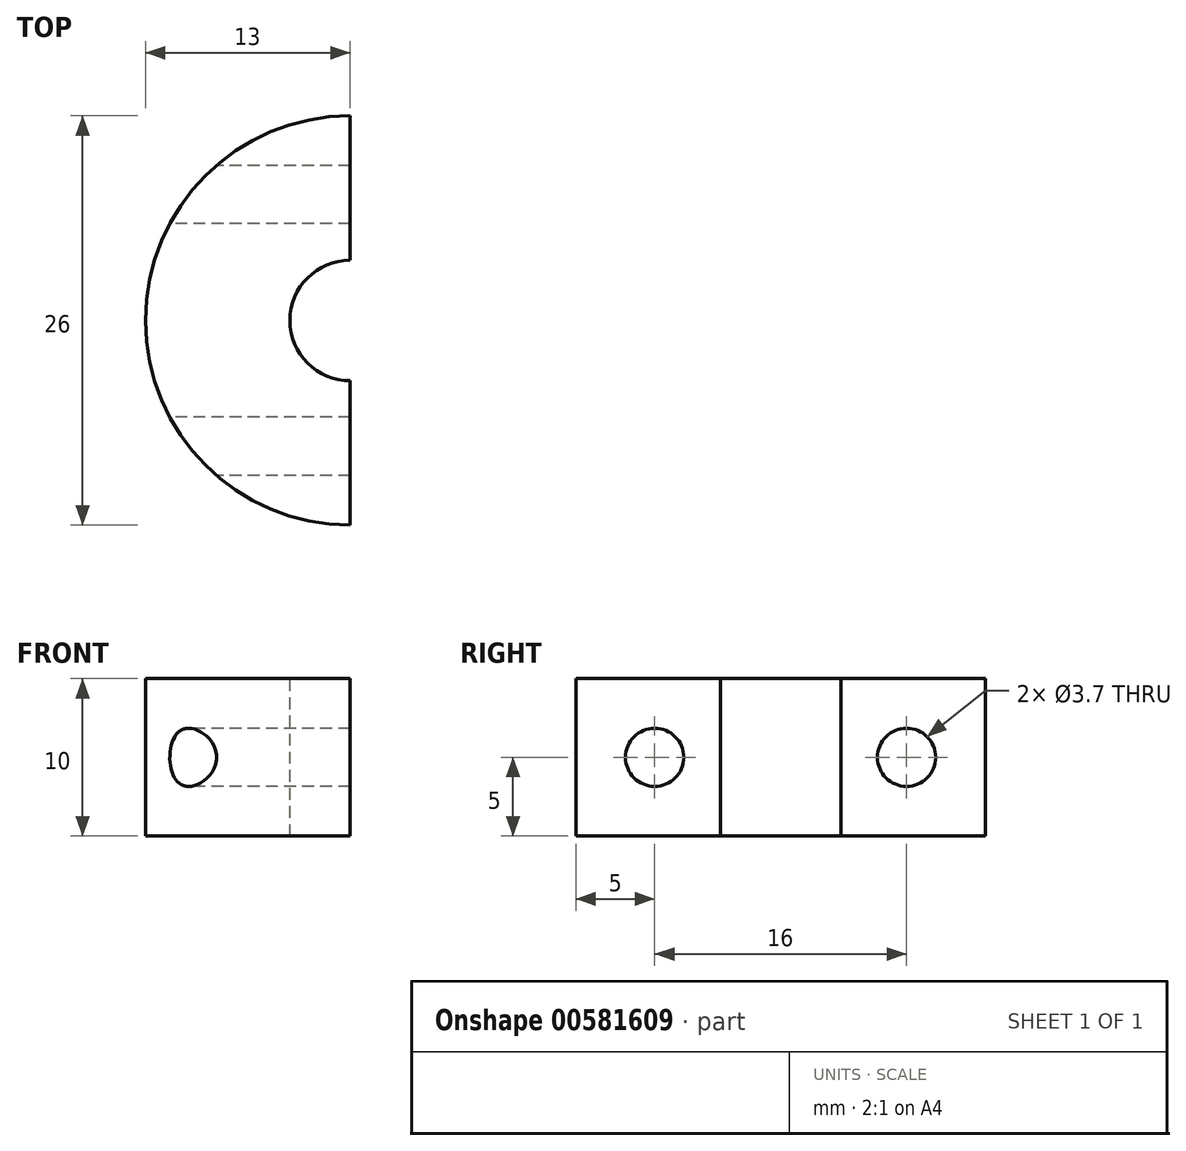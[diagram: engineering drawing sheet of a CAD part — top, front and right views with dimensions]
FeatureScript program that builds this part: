
annotation { "Feature Type Name" : "Feature", "Feature Type Description" : "" }
export const myFeature = defineFeature(function(context is Context, id is Id, definition is map)
    precondition{}
    {
        {
            var Q0;
            Q0=qCreatedBy(makeId("Top.planeOp"),FACE);
            var sketch = newSketch(context, id + "F0", { "sketchPlane" : qUnion([Q0])});
            skLineSegment(sketch, "E0.bottom", {"start": v(-13, 13) * mm, "end": v(0, 13) * mm});
            skLineSegment(sketch, "E0.top", {"start": v(-13, -13) * mm, "end": v(0, -13) * mm});
            skLineSegment(sketch, "E0.left", {"start": v(-13, 13) * mm, "end": v(-13, -13) * mm});
            skArc(sketch, "E1", {"start": v(0, 3.82) * mm, "mid": v(-3.82, 0) * mm, "end": v(0, -3.82) * mm});
            skLineSegment(sketch, "E2", {"start": v(0, 20.39) * mm, "end": v(0, -13) * mm});
            skLineSegment(sketch, "E3", {"start": v(-6.2, 18.83) * mm, "end": v(-6.2, -11.9) * mm});
            skLineSegment(sketch, "E4", {"start": v(-27.69, 6.5) * mm, "end": v(10.91, 6.5) * mm});
            skLineSegment(sketch, "E5", {"start": v(-23.22, -6.5) * mm, "end": v(13.32, -6.5) * mm});
            skSolve(sketch);
        }
        {
            var Q0;
            {var subQ0=sQuery(id+"F0.wireOp",EDGE,"E4");var subQ1=sQuery(id+"F0.wireOp",EDGE,"ij9M0F4P-wxEO-HOR3-qSz0-gCgoNjpAj9Vk");var subQ2=makeQuery(id+"F0.imprint","INTERSECT",VERTEX,{"derivedFrom":[subQ1,subQ0]});Q0=makeQuery(id+"F0.imprint","IMPRINT",FACE,{"disambiguationData":[TD([[makeQuery(id+"F0.imprint","IMPRINT",EDGE,{"disambiguationData":[TD([[subQ2,-1.0]])],"derivedFrom":subQ1}),1.0]])]});}
            var Q1;
            {var subQ1=sQuery(id+"F0.wireOp",EDGE,"E1");Q1=makeQuery(id+"F0.imprint","IMPRINT",FACE,{"disambiguationData":[TD([[makeQuery(id+"F0.imprint","IMPRINT",EDGE,{"derivedFrom":subQ1}),-1.0]])]});}
            var Q2;
            {var subQ0=sQuery(id+"F0.wireOp",EDGE,"E2");var subQ1=sQuery(id+"F0.wireOp",EDGE,"ij9M0F4P-wxEO-HOR3-qSz0-gCgoNjpAj9Vk");var subQ2=makeQuery(id+"F0.imprint","INTERSECT",VERTEX,{"disambiguationData":[OD(0.0)],"derivedFrom":[subQ1,subQ0]});Q2=makeQuery(id+"F0.imprint","IMPRINT",FACE,{"disambiguationData":[TD([[makeQuery(id+"F0.imprint","IMPRINT",EDGE,{"disambiguationData":[TD([[subQ2,-1.0]])],"derivedFrom":subQ1}),1.0]])]});}
            var Q3;
            {var subQ0=sQuery(id+"F0.wireOp",EDGE,"E2");var subQ1=sQuery(id+"F0.wireOp",EDGE,"ij9M0F4P-wxEO-HOR3-qSz0-gCgoNjpAj9Vk");var subQ2=makeQuery(id+"F0.imprint","INTERSECT",VERTEX,{"disambiguationData":[OD(1.0)],"derivedFrom":[subQ1,subQ0]});Q3=makeQuery(id+"F0.imprint","IMPRINT",FACE,{"disambiguationData":[TD([[makeQuery(id+"F0.imprint","IMPRINT",EDGE,{"disambiguationData":[TD([[subQ2,1.0]])],"derivedFrom":subQ1}),1.0]])]});}
            var Q4;
            {var subQ0=sQuery(id+"F0.wireOp",EDGE,"E4");var subQ1=sQuery(id+"F0.wireOp",EDGE,"E0.left");var subQ2=makeQuery(id+"F0.imprint","INTERSECT",VERTEX,{"derivedFrom":[subQ1,subQ0]});Q4=makeQuery(id+"F0.imprint","IMPRINT",FACE,{"disambiguationData":[TD([[makeQuery(id+"F0.imprint","IMPRINT",EDGE,{"disambiguationData":[TD([[subQ2,-1.0]])],"derivedFrom":subQ1}),1.0]])]});}
            var Q5;
            {var subQ5=sQuery(id+"F0.wireOp",EDGE,"E0.bottom");var subQ7=sQuery(id+"F0.wireOp",EDGE,"E0.left");var subQ8=makeQuery(id+"F0.imprint","INTERSECT",VERTEX,{"derivedFrom":[subQ5,subQ7]});Q5=makeQuery(id+"F0.imprint","IMPRINT",FACE,{"disambiguationData":[TD([[makeQuery(id+"F0.imprint","IMPRINT",EDGE,{"disambiguationData":[TD([[subQ8,-1.0]])],"derivedFrom":subQ5}),-1.0]])]});}
            var Q6;
            {var subQ0=sQuery(id+"F0.wireOp",EDGE,"E2");var subQ1=sQuery(id+"F0.wireOp",EDGE,"E0.bottom");var subQ2=makeQuery(id+"F0.imprint","INTERSECT",VERTEX,{"derivedFrom":[subQ1,subQ0]});Q6=makeQuery(id+"F0.imprint","IMPRINT",FACE,{"disambiguationData":[TD([[makeQuery(id+"F0.imprint","IMPRINT",EDGE,{"disambiguationData":[TD([[subQ2,1.0]])],"derivedFrom":subQ1}),-1.0]])]});}
            var Q7;
            {var subQ1=sQuery(id+"F0.wireOp",EDGE,"E0.top");var subQ5=sQuery(id+"F0.wireOp",EDGE,"E0.left");var subQ6=makeQuery(id+"F0.imprint","INTERSECT",VERTEX,{"derivedFrom":[subQ1,subQ5]});Q7=makeQuery(id+"F0.imprint","IMPRINT",FACE,{"disambiguationData":[TD([[makeQuery(id+"F0.imprint","IMPRINT",EDGE,{"disambiguationData":[TD([[subQ6,-1.0]])],"derivedFrom":subQ1}),1.0]])]});}
            var Q8;
            {var subQ0=sQuery(id+"F0.wireOp",EDGE,"E2");var subQ1=sQuery(id+"F0.wireOp",EDGE,"E0.top");var subQ2=makeQuery(id+"F0.imprint","INTERSECT",VERTEX,{"derivedFrom":[subQ1,subQ0]});Q8=makeQuery(id+"F0.imprint","IMPRINT",FACE,{"disambiguationData":[TD([[makeQuery(id+"F0.imprint","IMPRINT",EDGE,{"disambiguationData":[TD([[subQ2,1.0]])],"derivedFrom":subQ1}),1.0]])]});}
            extrude(context, id + "F1", {"entities" : qUnion([Q0, Q1, Q2, Q3, Q4, Q5, Q6, Q7, Q8]), "oppositeDirection" : true, "depth" : 10 * mm, "offsetDistance" : 25 * mm});
        }
        {
            var Q0;
            Q0=makeQuery(id+"F1.opExtrude","SWEPT_FACE",FACE,{"disambiguationData":[OSD([sQuery(id+"F0.wireOp",EDGE,"E0.left")])]});
            var sketch = newSketch(context, id + "F2", { "sketchPlane" : qUnion([Q0])});
            skCircle(sketch, "E6", {"center": v(-8, -5) * mm, "radius": 1.85 * mm});
            skCircle(sketch, "E7", {"center": v(8, -5) * mm, "radius": 1.85 * mm});
            skSolve(sketch);
        }
        {
            var Q0;
            Q0=makeQuery(id+"F2.imprint","IMPRINT",FACE,{"disambiguationData":[TD([[makeQuery(id+"F2.imprint","IMPRINT",EDGE,{"derivedFrom":sQuery(id+"F2.wireOp",EDGE,"E6")}),1.0]])]});
            var Q1;
            Q1=makeQuery(id+"F2.imprint","IMPRINT",FACE,{"disambiguationData":[TD([[makeQuery(id+"F2.imprint","IMPRINT",EDGE,{"derivedFrom":sQuery(id+"F2.wireOp",EDGE,"E7")}),1.0]])]});
            extrude(context, id + "F3", {"entities" : qUnion([Q0, Q1]), "operationType" : NewBodyOperationType.REMOVE, "endBound" : BoundingType.UP_TO_NEXT, "oppositeDirection" : true, "depth" : 25 * mm, "offsetDistance" : 25 * mm});
        }
        {
            var Q0;
            Q0=makeQuery(id+"F1.opExtrude","SWEPT_EDGE",EDGE,{"disambiguationData":[OSD([sQuery(id+"F0.wireOp",EDGE,"E0.bottom"),sQuery(id+"F0.wireOp",EDGE,"E0.left")])]});
            var Q1;
            Q1=makeQuery(id+"F1.opExtrude","SWEPT_EDGE",EDGE,{"disambiguationData":[OSD([sQuery(id+"F0.wireOp",EDGE,"E0.top"),sQuery(id+"F0.wireOp",EDGE,"E0.left")])]});
            fillet(context, id + "F4", {"entities" : qUnion([Q0, Q1]), "radius" : 13 * mm, "tangentPropagation" : true, "allowEdgeOverflow" : false});
        }
    });
